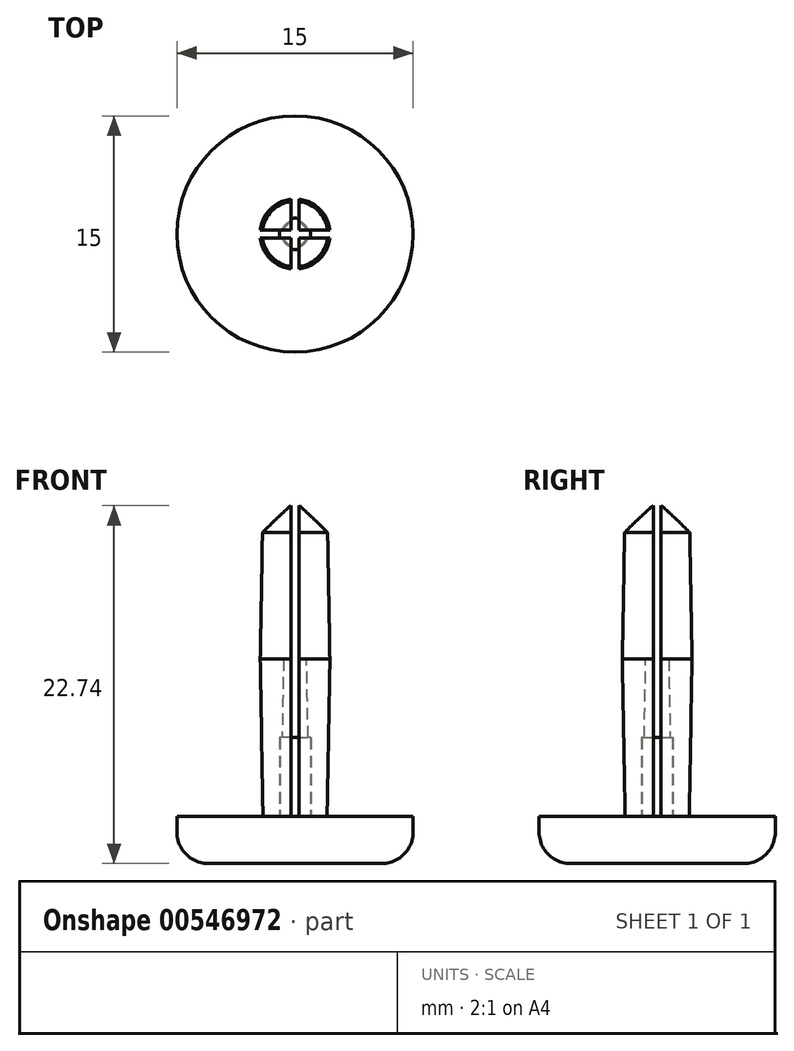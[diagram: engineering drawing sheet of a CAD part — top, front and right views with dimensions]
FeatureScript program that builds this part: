
annotation { "Feature Type Name" : "Feature", "Feature Type Description" : "" }
export const myFeature = defineFeature(function(context is Context, id is Id, definition is map)
    precondition{}
    {
        {
            var Q0;
            Q0=qCreatedBy(makeId("Top.planeOp"),FACE);
            var sketch = newSketch(context, id + "F0", { "sketchPlane" : qUnion([Q0])});
            skCircle(sketch, "E0", {"center": v(0, 0) * mm, "radius": 7.5 * mm});
            skCircle(sketch, "E1", {"center": v(0, 0) * mm, "radius": 2 * mm});
            skCircle(sketch, "E2", {"center": v(0, 0) * mm, "radius": 1 * mm});
            skSolve(sketch);
        }
        {
            var Q0;
            Q0=makeQuery(id+"F0.imprint","IMPRINT",FACE,{"disambiguationData":[TD([[makeQuery(id+"F0.imprint","IMPRINT",EDGE,{"derivedFrom":sQuery(id+"F0.wireOp",EDGE,"E0")}),1.0]])]});
            var Q1;
            {var subQ5=sQuery(id+"F0.wireOp",EDGE,"9Pv84VzD-bOTC-SwsB-n5Vm-WQtJVGXY80Nf.right");Q1=makeQuery(id+"F0.imprint","IMPRINT",FACE,{"disambiguationData":[TD([[makeQuery(id+"F0.imprint","IMPRINT",EDGE,{"derivedFrom":subQ5}),1.0]])]});}
            var Q2;
            {var subQ0=sQuery(id+"F0.wireOp",EDGE,"9Pv84VzD-bOTC-SwsB-n5Vm-WQtJVGXY80Nf.bottom");var subQ1=sQuery(id+"F0.wireOp",EDGE,"E1");var subQ2=makeQuery(id+"F0.imprint","INTERSECT",VERTEX,{"disambiguationData":[OD(1.0)],"derivedFrom":[subQ1,subQ0]});Q2=makeQuery(id+"F0.imprint","IMPRINT",FACE,{"disambiguationData":[TD([[makeQuery(id+"F0.imprint","IMPRINT",EDGE,{"disambiguationData":[TD([[subQ2,-1.0]])],"derivedFrom":subQ1}),1.0]])]});}
            var Q3;
            {var subQ0=sQuery(id+"F0.wireOp",EDGE,"pOMbJ7PC-GLTn-jcxA-tIG9-oSEWOmINgJHW.right");var subQ1=sQuery(id+"F0.wireOp",EDGE,"E1");var subQ2=makeQuery(id+"F0.imprint","INTERSECT",VERTEX,{"disambiguationData":[OD(0.0)],"derivedFrom":[subQ1,subQ0]});Q3=makeQuery(id+"F0.imprint","IMPRINT",FACE,{"disambiguationData":[TD([[makeQuery(id+"F0.imprint","IMPRINT",EDGE,{"disambiguationData":[TD([[subQ2,-1.0]])],"derivedFrom":subQ1}),1.0]])]});}
            var Q4;
            {var subQ0=sQuery(id+"F0.wireOp",EDGE,"pOMbJ7PC-GLTn-jcxA-tIG9-oSEWOmINgJHW.left");var subQ1=sQuery(id+"F0.wireOp",EDGE,"E1");var subQ2=makeQuery(id+"F0.imprint","INTERSECT",VERTEX,{"disambiguationData":[OD(0.0)],"derivedFrom":[subQ1,subQ0]});Q4=makeQuery(id+"F0.imprint","IMPRINT",FACE,{"disambiguationData":[TD([[makeQuery(id+"F0.imprint","IMPRINT",EDGE,{"disambiguationData":[TD([[subQ2,-1.0]])],"derivedFrom":subQ1}),1.0]])]});}
            var Q5;
            {var subQ5=sQuery(id+"F0.wireOp",EDGE,"pOMbJ7PC-GLTn-jcxA-tIG9-oSEWOmINgJHW.bottom");Q5=makeQuery(id+"F0.imprint","IMPRINT",FACE,{"disambiguationData":[TD([[makeQuery(id+"F0.imprint","IMPRINT",EDGE,{"derivedFrom":subQ5}),1.0]])]});}
            var Q6;
            {var subQ0=sQuery(id+"F0.wireOp",EDGE,"pOMbJ7PC-GLTn-jcxA-tIG9-oSEWOmINgJHW.left");var subQ1=sQuery(id+"F0.wireOp",EDGE,"E1");var subQ2=makeQuery(id+"F0.imprint","INTERSECT",VERTEX,{"disambiguationData":[OD(0.0)],"derivedFrom":[subQ1,subQ0]});Q6=makeQuery(id+"F0.imprint","IMPRINT",FACE,{"disambiguationData":[TD([[makeQuery(id+"F0.imprint","IMPRINT",EDGE,{"disambiguationData":[TD([[subQ2,1.0]])],"derivedFrom":subQ1}),1.0]])]});}
            var Q7;
            {var subQ0=sQuery(id+"F0.wireOp",EDGE,"9Pv84VzD-bOTC-SwsB-n5Vm-WQtJVGXY80Nf.bottom");var subQ1=sQuery(id+"F0.wireOp",EDGE,"E1");var subQ2=makeQuery(id+"F0.imprint","INTERSECT",VERTEX,{"disambiguationData":[OD(0.0)],"derivedFrom":[subQ1,subQ0]});Q7=makeQuery(id+"F0.imprint","IMPRINT",FACE,{"disambiguationData":[TD([[makeQuery(id+"F0.imprint","IMPRINT",EDGE,{"disambiguationData":[TD([[subQ2,1.0]])],"derivedFrom":subQ1}),1.0]])]});}
            var Q8;
            {var subQ0=sQuery(id+"F0.wireOp",EDGE,"pOMbJ7PC-GLTn-jcxA-tIG9-oSEWOmINgJHW.left");var subQ1=sQuery(id+"F0.wireOp",EDGE,"E1");var subQ2=makeQuery(id+"F0.imprint","INTERSECT",VERTEX,{"disambiguationData":[OD(1.0)],"derivedFrom":[subQ1,subQ0]});Q8=makeQuery(id+"F0.imprint","IMPRINT",FACE,{"disambiguationData":[TD([[makeQuery(id+"F0.imprint","IMPRINT",EDGE,{"disambiguationData":[TD([[subQ2,-1.0]])],"derivedFrom":subQ1}),1.0]])]});}
            var Q9;
            {var subQ5=sQuery(id+"F0.wireOp",EDGE,"9Pv84VzD-bOTC-SwsB-n5Vm-WQtJVGXY80Nf.left");Q9=makeQuery(id+"F0.imprint","IMPRINT",FACE,{"disambiguationData":[TD([[makeQuery(id+"F0.imprint","IMPRINT",EDGE,{"derivedFrom":subQ5}),-1.0]])]});}
            var Q10;
            {var subQ0=sQuery(id+"F0.wireOp",EDGE,"E2");var subQ1=sQuery(id+"F0.wireOp",EDGE,"9Pv84VzD-bOTC-SwsB-n5Vm-WQtJVGXY80Nf.bottom");var subQ2=makeQuery(id+"F0.imprint","INTERSECT",VERTEX,{"disambiguationData":[OD(0.0)],"derivedFrom":[subQ1,subQ0]});Q10=makeQuery(id+"F0.imprint","IMPRINT",FACE,{"disambiguationData":[TD([[makeQuery(id+"F0.imprint","IMPRINT",EDGE,{"disambiguationData":[TD([[subQ2,-1.0]])],"derivedFrom":subQ1}),1.0]])]});}
            var Q11;
            {var subQ0=sQuery(id+"F0.wireOp",EDGE,"E2");var subQ1=sQuery(id+"F0.wireOp",EDGE,"9Pv84VzD-bOTC-SwsB-n5Vm-WQtJVGXY80Nf.bottom");var subQ2=makeQuery(id+"F0.imprint","INTERSECT",VERTEX,{"disambiguationData":[OD(0.0)],"derivedFrom":[subQ1,subQ0]});Q11=makeQuery(id+"F0.imprint","IMPRINT",FACE,{"disambiguationData":[TD([[makeQuery(id+"F0.imprint","IMPRINT",EDGE,{"disambiguationData":[TD([[subQ2,-1.0]])],"derivedFrom":subQ1}),-1.0]])]});}
            var Q12;
            {var subQ0=sQuery(id+"F0.wireOp",EDGE,"pOMbJ7PC-GLTn-jcxA-tIG9-oSEWOmINgJHW.left");var subQ1=sQuery(id+"F0.wireOp",EDGE,"9Pv84VzD-bOTC-SwsB-n5Vm-WQtJVGXY80Nf.bottom");var subQ2=makeQuery(id+"F0.imprint","INTERSECT",VERTEX,{"derivedFrom":[subQ1,subQ0]});Q12=makeQuery(id+"F0.imprint","IMPRINT",FACE,{"disambiguationData":[TD([[makeQuery(id+"F0.imprint","IMPRINT",EDGE,{"disambiguationData":[TD([[subQ2,-1.0]])],"derivedFrom":subQ1}),-1.0]])]});}
            var Q13;
            {var subQ0=sQuery(id+"F0.wireOp",EDGE,"pOMbJ7PC-GLTn-jcxA-tIG9-oSEWOmINgJHW.right");var subQ1=sQuery(id+"F0.wireOp",EDGE,"9Pv84VzD-bOTC-SwsB-n5Vm-WQtJVGXY80Nf.bottom");var subQ2=makeQuery(id+"F0.imprint","INTERSECT",VERTEX,{"derivedFrom":[subQ1,subQ0]});Q13=makeQuery(id+"F0.imprint","IMPRINT",FACE,{"disambiguationData":[TD([[makeQuery(id+"F0.imprint","IMPRINT",EDGE,{"disambiguationData":[TD([[subQ2,-1.0]])],"derivedFrom":subQ1}),-1.0]])]});}
            var Q14;
            {var subQ0=sQuery(id+"F0.wireOp",EDGE,"pOMbJ7PC-GLTn-jcxA-tIG9-oSEWOmINgJHW.right");var subQ1=sQuery(id+"F0.wireOp",EDGE,"9Pv84VzD-bOTC-SwsB-n5Vm-WQtJVGXY80Nf.bottom");var subQ2=makeQuery(id+"F0.imprint","INTERSECT",VERTEX,{"derivedFrom":[subQ1,subQ0]});Q14=makeQuery(id+"F0.imprint","IMPRINT",FACE,{"disambiguationData":[TD([[makeQuery(id+"F0.imprint","IMPRINT",EDGE,{"disambiguationData":[TD([[subQ2,-1.0]])],"derivedFrom":subQ1}),1.0]])]});}
            var Q15;
            {var subQ0=sQuery(id+"F0.wireOp",EDGE,"9Pv84VzD-bOTC-SwsB-n5Vm-WQtJVGXY80Nf.top");var subQ1=sQuery(id+"F0.wireOp",EDGE,"E1");var subQ2=makeQuery(id+"F0.imprint","INTERSECT",VERTEX,{"disambiguationData":[OD(0.0)],"derivedFrom":[subQ1,subQ0]});Q15=makeQuery(id+"F0.imprint","IMPRINT",FACE,{"disambiguationData":[TD([[makeQuery(id+"F0.imprint","IMPRINT",EDGE,{"disambiguationData":[TD([[subQ2,-1.0]])],"derivedFrom":subQ1}),1.0]])]});}
            var Q16;
            {var subQ0=sQuery(id+"F0.wireOp",EDGE,"pOMbJ7PC-GLTn-jcxA-tIG9-oSEWOmINgJHW.right");var subQ1=sQuery(id+"F0.wireOp",EDGE,"9Pv84VzD-bOTC-SwsB-n5Vm-WQtJVGXY80Nf.top");var subQ2=makeQuery(id+"F0.imprint","INTERSECT",VERTEX,{"derivedFrom":[subQ1,subQ0]});Q16=makeQuery(id+"F0.imprint","IMPRINT",FACE,{"disambiguationData":[TD([[makeQuery(id+"F0.imprint","IMPRINT",EDGE,{"disambiguationData":[TD([[subQ2,-1.0]])],"derivedFrom":subQ1}),1.0]])]});}
            var Q17;
            {var subQ0=sQuery(id+"F0.wireOp",EDGE,"pOMbJ7PC-GLTn-jcxA-tIG9-oSEWOmINgJHW.left");var subQ1=sQuery(id+"F0.wireOp",EDGE,"9Pv84VzD-bOTC-SwsB-n5Vm-WQtJVGXY80Nf.top");var subQ2=makeQuery(id+"F0.imprint","INTERSECT",VERTEX,{"derivedFrom":[subQ1,subQ0]});Q17=makeQuery(id+"F0.imprint","IMPRINT",FACE,{"disambiguationData":[TD([[makeQuery(id+"F0.imprint","IMPRINT",EDGE,{"disambiguationData":[TD([[subQ2,-1.0]])],"derivedFrom":subQ1}),1.0]])]});}
            var Q18;
            {var subQ0=sQuery(id+"F0.wireOp",EDGE,"E2");var subQ1=sQuery(id+"F0.wireOp",EDGE,"9Pv84VzD-bOTC-SwsB-n5Vm-WQtJVGXY80Nf.top");var subQ2=makeQuery(id+"F0.imprint","INTERSECT",VERTEX,{"disambiguationData":[OD(0.0)],"derivedFrom":[subQ1,subQ0]});Q18=makeQuery(id+"F0.imprint","IMPRINT",FACE,{"disambiguationData":[TD([[makeQuery(id+"F0.imprint","IMPRINT",EDGE,{"disambiguationData":[TD([[subQ2,-1.0]])],"derivedFrom":subQ1}),1.0]])]});}
            var Q19;
            {var subQ0=sQuery(id+"F0.wireOp",EDGE,"pOMbJ7PC-GLTn-jcxA-tIG9-oSEWOmINgJHW.right");var subQ1=sQuery(id+"F0.wireOp",EDGE,"E1");var subQ2=makeQuery(id+"F0.imprint","INTERSECT",VERTEX,{"disambiguationData":[OD(1.0)],"derivedFrom":[subQ1,subQ0]});Q19=makeQuery(id+"F0.imprint","IMPRINT",FACE,{"disambiguationData":[TD([[makeQuery(id+"F0.imprint","IMPRINT",EDGE,{"disambiguationData":[TD([[subQ2,-1.0]])],"derivedFrom":subQ1}),1.0]])]});}
            var Q20;
            {var subQ0=sQuery(id+"F0.wireOp",EDGE,"pOMbJ7PC-GLTn-jcxA-tIG9-oSEWOmINgJHW.left");var subQ1=sQuery(id+"F0.wireOp",EDGE,"9Pv84VzD-bOTC-SwsB-n5Vm-WQtJVGXY80Nf.bottom");var subQ2=makeQuery(id+"F0.imprint","INTERSECT",VERTEX,{"derivedFrom":[subQ1,subQ0]});Q20=makeQuery(id+"F0.imprint","IMPRINT",FACE,{"disambiguationData":[TD([[makeQuery(id+"F0.imprint","IMPRINT",EDGE,{"disambiguationData":[TD([[subQ2,-1.0]])],"derivedFrom":subQ1}),1.0]])]});}
            var Q21;
            {var subQ5=sQuery(id+"F0.wireOp",EDGE,"pOMbJ7PC-GLTn-jcxA-tIG9-oSEWOmINgJHW.top");Q21=makeQuery(id+"F0.imprint","IMPRINT",FACE,{"disambiguationData":[TD([[makeQuery(id+"F0.imprint","IMPRINT",EDGE,{"derivedFrom":subQ5}),-1.0]])]});}
            var Q22;
            Q22=makeQuery(id+"F0.imprint","IMPRINT",FACE,{"disambiguationData":[TD([[makeQuery(id+"F0.imprint","IMPRINT",EDGE,{"derivedFrom":sQuery(id+"F0.wireOp",EDGE,"E2")}),1.0]])]});
            var Q23;
            Q23=makeQuery(id+"F0.imprint","IMPRINT",FACE,{"disambiguationData":[TD([[makeQuery(id+"F0.imprint","IMPRINT",EDGE,{"derivedFrom":sQuery(id+"F0.wireOp",EDGE,"E1")}),1.0]])]});
            extrude(context, id + "F1", {"entities" : qUnion([Q0, Q1, Q2, Q3, Q4, Q5, Q6, Q7, Q8, Q9, Q10, Q11, Q12, Q13, Q14, Q15, Q16, Q17, Q18, Q19, Q20, Q21, Q22, Q23]), "depth" : 3 * mm, "offsetDistance" : 25 * mm});
        }
        {
            var Q0;
            Q0=makeQuery(id+"F0.imprint","IMPRINT",FACE,{"disambiguationData":[TD([[makeQuery(id+"F0.imprint","IMPRINT",EDGE,{"derivedFrom":sQuery(id+"F0.wireOp",EDGE,"E1")}),1.0]])]});
            extrude(context, id + "F2", {"entities" : qUnion([Q0]), "operationType" : NewBodyOperationType.ADD, "depth" : 13 * mm, "offsetDistance" : 25 * mm, "hasDraft" : true, "draftAngle" : 1 * degree});
        }
        {
            var Q0;
            Q0=makeQuery(id+"F1.opExtrude","CAP_EDGE",EDGE,{"disambiguationData":[OSD([sQuery(id+"F0.wireOp",EDGE,"E0")])],"isStart":true});
            fillet(context, id + "F3", {"entities" : qUnion([Q0]), "radius" : 2 * mm, "tangentPropagation" : true, "allowEdgeOverflow" : false});
        }
        {
            var Q0;
            {var subQ0=sQuery(id+"F0.wireOp",EDGE,"E0");Q0=makeQuery(id+"F2.boolean.opBoolean","SPLIT",FACE,{"disambiguationData":[TD([makeQuery(id+"F1.opExtrude","SWEPT_FACE",FACE,{"disambiguationData":[OSD([subQ0])]})])],"derivedFrom":makeQuery(id+"F1.opExtrude","CAP_FACE",FACE,{"disambiguationData":[OSD([subQ0])],"isStart":false})});}
            var sketch = newSketch(context, id + "F4", { "sketchPlane" : qUnion([Q0])});
            skLineSegment(sketch, "E3.bottom", {"start": v(4.28, 0.25) * mm, "end": v(-4.28, 0.25) * mm});
            skLineSegment(sketch, "E3.top", {"start": v(4.28, -0.25) * mm, "end": v(-4.28, -0.25) * mm});
            skLineSegment(sketch, "E3.left", {"start": v(4.28, 0.25) * mm, "end": v(4.28, -0.25) * mm});
            skLineSegment(sketch, "E3.right", {"start": v(-4.28, 0.25) * mm, "end": v(-4.28, -0.25) * mm});
            skPoint(sketch, "E3.middle", {"position": v(0, 0) * mm});
            skLineSegment(sketch, "E4.bottom", {"start": v(0.25, -4.62) * mm, "end": v(-0.25, -4.62) * mm});
            skLineSegment(sketch, "E4.top", {"start": v(0.25, 4.62) * mm, "end": v(-0.25, 4.62) * mm});
            skLineSegment(sketch, "E4.left", {"start": v(0.25, -4.62) * mm, "end": v(0.25, 4.62) * mm});
            skLineSegment(sketch, "E4.right", {"start": v(-0.25, -4.62) * mm, "end": v(-0.25, 4.62) * mm});
            skSolve(sketch);
        }
        {
            var Q0;
            {var subQ0=sQuery(id+"F0.wireOp",EDGE,"E1");var subQ2=sQuery(id+"F4.wireOp",EDGE,"E4.right");var subQ3=sQuery(id+"F4.wireOp",EDGE,"E3.top");var subQ4=makeQuery(id+"F4.imprint","INTERSECT",VERTEX,{"derivedFrom":[subQ3,subQ2]});var subQ7=sQuery(id+"F0.wireOp",EDGE,"E2");Q0=makeQuery(id+"F7.boolean.opBoolean","SPLIT",FACE,{"disambiguationData":[TD([makeQuery(id+"F7.opExtrude","SWEPT_FACE",FACE,{"disambiguationData":[OSD([subQ3]),TDD([makeQuery(id+"F4.imprint","IMPRINT",EDGE,{"disambiguationData":[TD([[subQ4,-1.0]])],"derivedFrom":subQ3}),makeQuery(id+"F4.imprint","IMPRINT",EDGE,{"disambiguationData":[TD([[makeQuery(id+"F4.imprint","INTERSECT",VERTEX,{"derivedFrom":[subQ3,sQuery(id+"F4.wireOp",EDGE,"E3.right")]}),1.0]])],"derivedFrom":subQ3})])]})])],"derivedFrom":makeQuery(id+"F2.opExtrude","CAP_FACE",FACE,{"disambiguationData":[OSD([subQ0,subQ7])],"isStart":false})});}
            var sketch = newSketch(context, id + "F5", { "sketchPlane" : qUnion([Q0])});
            skCircle(sketch, "E5", {"center": v(0, 0) * mm, "radius": 2.23 * mm});
            skSolve(sketch);
        }
        {
            var Q0;
            Q0 = qSketchRegion(id + "F5", true);
            extrude(context, id + "F6", {"entities" : qUnion([Q0]), "operationType" : NewBodyOperationType.ADD, "depth" : 10 * mm, "offsetDistance" : 25 * mm, "hasDraft" : true, "draftAngle" : 1 * degree, "draftPullDirection" : true});
        }
        {
            var Q0;
            Q0 = qSketchRegion(id + "F4", true);
            extrude(context, id + "F7", {"entities" : qUnion([Q0]), "operationType" : NewBodyOperationType.REMOVE, "endBound" : BoundingType.THROUGH_ALL, "depth" : 25 * mm, "offsetDistance" : 25 * mm});
        }
        {
            var Q0;
            Q0=makeQuery(id+"F0.imprint","IMPRINT",FACE,{"disambiguationData":[TD([[makeQuery(id+"F0.imprint","IMPRINT",EDGE,{"derivedFrom":sQuery(id+"F0.wireOp",EDGE,"E2")}),1.0]])]});
            extrude(context, id + "F8", {"entities" : qUnion([Q0]), "operationType" : NewBodyOperationType.ADD, "depth" : 8 * mm, "offsetDistance" : 25 * mm});
        }
        {
            var Q0;
            {var subQ0=sQuery(id+"F5.wireOp",EDGE,"E5");var subQ1=sQuery(id+"F4.wireOp",EDGE,"E3.top");var subQ4=sQuery(id+"F4.wireOp",EDGE,"E4.right");var subQ5=makeQuery(id+"F4.imprint","INTERSECT",VERTEX,{"derivedFrom":[subQ1,subQ4]});Q0=makeQuery(id+"F7.boolean.opBoolean","SPLIT",EDGE,{"disambiguationData":[TD([makeQuery(id+"F7.opExtrude","SWEPT_FACE",FACE,{"disambiguationData":[OSD([subQ1]),TDD([makeQuery(id+"F4.imprint","IMPRINT",EDGE,{"disambiguationData":[TD([[subQ5,-1.0]])],"derivedFrom":subQ1}),makeQuery(id+"F4.imprint","IMPRINT",EDGE,{"disambiguationData":[TD([[makeQuery(id+"F4.imprint","INTERSECT",VERTEX,{"derivedFrom":[subQ1,sQuery(id+"F4.wireOp",EDGE,"E3.right")]}),1.0]])],"derivedFrom":subQ1})])]})])],"derivedFrom":makeQuery(id+"F6.opExtrude","CAP_EDGE",EDGE,{"disambiguationData":[OSD([subQ0])],"isStart":false})});}
            var Q1;
            {var subQ0=sQuery(id+"F5.wireOp",EDGE,"E5");var subQ1=sQuery(id+"F4.wireOp",EDGE,"E4.left");var subQ2=sQuery(id+"F4.wireOp",EDGE,"E3.top");var subQ3=makeQuery(id+"F4.imprint","INTERSECT",VERTEX,{"derivedFrom":[subQ2,subQ1]});Q1=makeQuery(id+"F7.boolean.opBoolean","SPLIT",EDGE,{"disambiguationData":[TD([makeQuery(id+"F7.opExtrude","SWEPT_FACE",FACE,{"disambiguationData":[OSD([subQ2]),TDD([makeQuery(id+"F4.imprint","IMPRINT",EDGE,{"disambiguationData":[TD([[makeQuery(id+"F4.imprint","INTERSECT",VERTEX,{"derivedFrom":[subQ2,sQuery(id+"F4.wireOp",EDGE,"E3.left")]}),-1.0]])],"derivedFrom":subQ2}),makeQuery(id+"F4.imprint","IMPRINT",EDGE,{"disambiguationData":[TD([[subQ3,1.0]])],"derivedFrom":subQ2})])]})])],"derivedFrom":makeQuery(id+"F6.opExtrude","CAP_EDGE",EDGE,{"disambiguationData":[OSD([subQ0])],"isStart":false})});}
            var Q2;
            {var subQ0=sQuery(id+"F5.wireOp",EDGE,"E5");var subQ1=sQuery(id+"F4.wireOp",EDGE,"E4.left");var subQ2=sQuery(id+"F4.wireOp",EDGE,"E3.bottom");var subQ3=makeQuery(id+"F4.imprint","INTERSECT",VERTEX,{"derivedFrom":[subQ2,subQ1]});Q2=makeQuery(id+"F7.boolean.opBoolean","SPLIT",EDGE,{"disambiguationData":[TD([makeQuery(id+"F7.opExtrude","SWEPT_FACE",FACE,{"disambiguationData":[OSD([subQ2]),TDD([makeQuery(id+"F4.imprint","IMPRINT",EDGE,{"disambiguationData":[TD([[makeQuery(id+"F4.imprint","INTERSECT",VERTEX,{"derivedFrom":[subQ2,sQuery(id+"F4.wireOp",EDGE,"E3.left")]}),-1.0]])],"derivedFrom":subQ2}),makeQuery(id+"F4.imprint","IMPRINT",EDGE,{"disambiguationData":[TD([[subQ3,1.0]])],"derivedFrom":subQ2})])]})])],"derivedFrom":makeQuery(id+"F6.opExtrude","CAP_EDGE",EDGE,{"disambiguationData":[OSD([subQ0])],"isStart":false})});}
            var Q3;
            {var subQ0=sQuery(id+"F5.wireOp",EDGE,"E5");var subQ1=sQuery(id+"F4.wireOp",EDGE,"E3.bottom");var subQ4=sQuery(id+"F4.wireOp",EDGE,"E4.right");var subQ5=makeQuery(id+"F4.imprint","INTERSECT",VERTEX,{"derivedFrom":[subQ1,subQ4]});Q3=makeQuery(id+"F7.boolean.opBoolean","SPLIT",EDGE,{"disambiguationData":[TD([makeQuery(id+"F7.opExtrude","SWEPT_FACE",FACE,{"disambiguationData":[OSD([subQ1]),TDD([makeQuery(id+"F4.imprint","IMPRINT",EDGE,{"disambiguationData":[TD([[subQ5,-1.0]])],"derivedFrom":subQ1}),makeQuery(id+"F4.imprint","IMPRINT",EDGE,{"disambiguationData":[TD([[makeQuery(id+"F4.imprint","INTERSECT",VERTEX,{"derivedFrom":[subQ1,sQuery(id+"F4.wireOp",EDGE,"E3.right")]}),1.0]])],"derivedFrom":subQ1})])]})])],"derivedFrom":makeQuery(id+"F6.opExtrude","CAP_EDGE",EDGE,{"disambiguationData":[OSD([subQ0])],"isStart":false})});}
            chamfer(context, id + "F9", {"entities" : qUnion([Q0, Q1, Q2, Q3]), "width" : 2 * mm, "tangentPropagation" : true});
        }
    });
